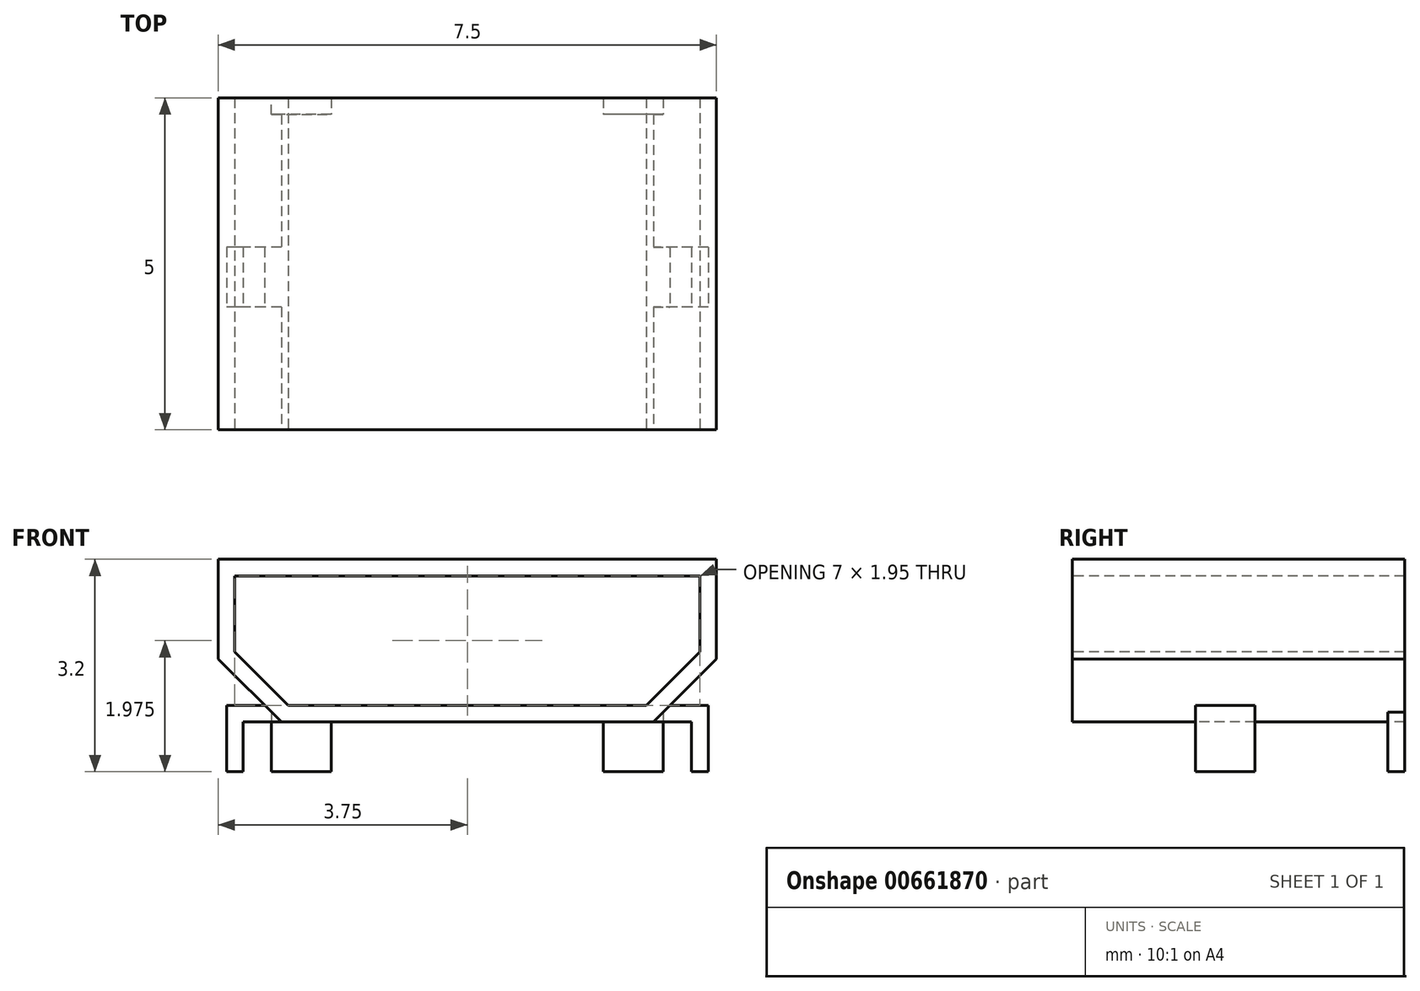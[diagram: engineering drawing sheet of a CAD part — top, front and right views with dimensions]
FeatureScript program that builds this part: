
annotation { "Feature Type Name" : "Feature", "Feature Type Description" : "" }
export const myFeature = defineFeature(function(context is Context, id is Id, definition is map)
    precondition{}
    {
        {
            var Q0;
            Q0=qCreatedBy(makeId("Front.planeOp"),FACE);
            var sketch = newSketch(context, id + "F0", { "sketchPlane" : qUnion([Q0])});
            skLineSegment(sketch, "E0", {"start": v(0, 0) * mm, "end": v(2.8, 0) * mm});
            skLineSegment(sketch, "E1", {"start": v(2.8, 0) * mm, "end": v(3.75, 0.95) * mm});
            skLineSegment(sketch, "E2", {"start": v(3.75, 0.95) * mm, "end": v(3.75, 2.45) * mm});
            skLineSegment(sketch, "E3", {"start": v(3.75, 2.45) * mm, "end": v(0, 2.45) * mm});
            skLineSegment(sketch, "E4", {"start": v(0, 2.45) * mm, "end": v(0, 5.13) * mm, "construction": true});
            skLineSegment(sketch, "E5.0", {"start": v(3.5, 2.2) * mm, "end": v(0, 2.2) * mm});
            skLineSegment(sketch, "E5.1", {"start": v(3.5, 1.05) * mm, "end": v(3.5, 2.2) * mm});
            skLineSegment(sketch, "E5.2", {"start": v(2.7, 0.25) * mm, "end": v(3.5, 1.05) * mm});
            skLineSegment(sketch, "E5.3", {"start": v(0, 0.25) * mm, "end": v(2.7, 0.25) * mm});
            skLineSegment(sketch, "E6.MirrorCS", {"start": v(-3.75, 2.45) * mm, "end": v(0, 2.45) * mm});
            skLineSegment(sketch, "E7.MirrorCS", {"start": v(-3.5, 2.2) * mm, "end": v(0, 2.2) * mm});
            skLineSegment(sketch, "E8.MirrorCS", {"start": v(-3.5, 1.05) * mm, "end": v(-3.5, 2.2) * mm});
            skLineSegment(sketch, "E9.MirrorCS", {"start": v(-3.75, 0.95) * mm, "end": v(-3.75, 2.45) * mm});
            skLineSegment(sketch, "E10.MirrorCS", {"start": v(-2.7, 0.25) * mm, "end": v(-3.5, 1.05) * mm});
            skLineSegment(sketch, "E11.MirrorCS", {"start": v(-2.8, 0) * mm, "end": v(-3.75, 0.95) * mm});
            skLineSegment(sketch, "E12.MirrorCS", {"start": v(0, 0.25) * mm, "end": v(-2.7, 0.25) * mm});
            skLineSegment(sketch, "E13.MirrorCS", {"start": v(0, 0) * mm, "end": v(-2.8, 0) * mm});
            skLineSegment(sketch, "E14", {"start": v(0, 2.2) * mm, "end": v(0, 0.25) * mm, "construction": true});
            skCircle(sketch, "E15", {"center": v(0, 1.23) * mm, "radius": 0.97 * mm, "construction": true});
            skSolve(sketch);
        }
        {
            var Q0;
            Q0=makeQuery(id+"F0.imprint","IMPRINT",FACE,{"disambiguationData":[TD([[makeQuery(id+"F0.imprint","IMPRINT",EDGE,{"derivedFrom":sQuery(id+"F0.wireOp",EDGE,"E0")}),1.0]])]});
            extrude(context, id + "F1", {"entities" : qUnion([Q0]), "oppositeDirection" : true, "depth" : 5 * mm, "offsetDistance" : 25 * mm});
        }
        {
            var Q0;
            Q0=makeQuery(id+"F1.opExtrude","CAP_FACE",FACE,{"disambiguationData":[OSD([sQuery(id+"F0.wireOp",EDGE,"E0"),sQuery(id+"F0.wireOp",EDGE,"E1"),sQuery(id+"F0.wireOp",EDGE,"E2"),sQuery(id+"F0.wireOp",EDGE,"E3"),sQuery(id+"F0.wireOp",EDGE,"E5.0"),sQuery(id+"F0.wireOp",EDGE,"E5.1"),sQuery(id+"F0.wireOp",EDGE,"E5.2"),sQuery(id+"F0.wireOp",EDGE,"E5.3"),sQuery(id+"F0.wireOp",EDGE,"E6.MirrorCS"),sQuery(id+"F0.wireOp",EDGE,"E7.MirrorCS"),sQuery(id+"F0.wireOp",EDGE,"E8.MirrorCS"),sQuery(id+"F0.wireOp",EDGE,"E9.MirrorCS"),sQuery(id+"F0.wireOp",EDGE,"E10.MirrorCS"),sQuery(id+"F0.wireOp",EDGE,"E11.MirrorCS"),sQuery(id+"F0.wireOp",EDGE,"E12.MirrorCS"),sQuery(id+"F0.wireOp",EDGE,"E13.MirrorCS")])],"isStart":false});
            cPlane(context, id + "F2", {"entities" : qUnion([Q0]), "cplaneType" : CPlaneType.OFFSET, "offset" : 2.7 * mm, "oppositeDirection" : true, "width" : 150 * mm, "height" : 150 * mm});
        }
        {
            var Q0;
            Q0=qCreatedBy(id+"F2.planeOp",FACE);
            var sketch = newSketch(context, id + "F3", { "sketchPlane" : qUnion([Q0])});
            skLineSegment(sketch, "E16", {"start": v(-3.62, -0.75) * mm, "end": v(-3.62, 0.25) * mm});
            skLineSegment(sketch, "E17", {"start": v(-3.62, 0.25) * mm, "end": v(3.62, 0.25) * mm});
            skLineSegment(sketch, "E18", {"start": v(3.62, 0.25) * mm, "end": v(3.62, -0.75) * mm});
            skLineSegment(sketch, "E19", {"start": v(0, 0) * mm, "end": v(0, -1.12) * mm, "construction": true});
            skLineSegment(sketch, "E20", {"start": v(-3.5, 0.25) * mm, "end": v(-3.5, -0.75) * mm, "construction": true});
            skLineSegment(sketch, "E21", {"start": v(-3.62, -0.75) * mm, "end": v(-3.38, -0.75) * mm});
            skLineSegment(sketch, "E22", {"start": v(-3.38, -0.75) * mm, "end": v(-3.38, 0) * mm});
            skLineSegment(sketch, "E23", {"start": v(-3.38, 0) * mm, "end": v(3.38, 0) * mm});
            skLineSegment(sketch, "E24", {"start": v(3.38, 0) * mm, "end": v(3.38, -0.75) * mm});
            skLineSegment(sketch, "E25", {"start": v(3.38, -0.75) * mm, "end": v(3.62, -0.75) * mm});
            skSolve(sketch);
        }
        {
            var Q0;
            Q0 = qSketchRegion(id + "F3", true);
            extrude(context, id + "F4", {"entities" : qUnion([Q0]), "operationType" : NewBodyOperationType.ADD, "depth" : 0.9 * mm, "offsetDistance" : 25 * mm, "symmetric" : true});
        }
        {
            var Q0;
            Q0=makeQuery(id+"F1.opExtrude","CAP_FACE",FACE,{"disambiguationData":[OSD([sQuery(id+"F0.wireOp",EDGE,"E0"),sQuery(id+"F0.wireOp",EDGE,"E1"),sQuery(id+"F0.wireOp",EDGE,"E2"),sQuery(id+"F0.wireOp",EDGE,"E3"),sQuery(id+"F0.wireOp",EDGE,"E5.0"),sQuery(id+"F0.wireOp",EDGE,"E5.1"),sQuery(id+"F0.wireOp",EDGE,"E5.2"),sQuery(id+"F0.wireOp",EDGE,"E5.3"),sQuery(id+"F0.wireOp",EDGE,"E6.MirrorCS"),sQuery(id+"F0.wireOp",EDGE,"E7.MirrorCS"),sQuery(id+"F0.wireOp",EDGE,"E8.MirrorCS"),sQuery(id+"F0.wireOp",EDGE,"E9.MirrorCS"),sQuery(id+"F0.wireOp",EDGE,"E10.MirrorCS"),sQuery(id+"F0.wireOp",EDGE,"E11.MirrorCS"),sQuery(id+"F0.wireOp",EDGE,"E12.MirrorCS"),sQuery(id+"F0.wireOp",EDGE,"E13.MirrorCS")])],"isStart":false});
            var sketch = newSketch(context, id + "F5", { "sketchPlane" : qUnion([Q0])});
            skLineSegment(sketch, "E26", {"start": v(-2.95, 0.25) * mm, "end": v(-2.95, -0.75) * mm});
            skLineSegment(sketch, "E27", {"start": v(-2.95, -0.75) * mm, "end": v(-2.05, -0.75) * mm});
            skLineSegment(sketch, "E28", {"start": v(-2.05, -0.75) * mm, "end": v(-2.05, 0.25) * mm});
            skLineSegment(sketch, "E29", {"start": v(-2.05, 0.25) * mm, "end": v(-2.95, 0.25) * mm});
            skLineSegment(sketch, "E30", {"start": v(0, 0) * mm, "end": v(0, -1) * mm, "construction": true});
            skLineSegment(sketch, "E31", {"start": v(-2.5, -0.75) * mm, "end": v(-2.5, 0.25) * mm, "construction": true});
            skLineSegment(sketch, "E32.MirrorCS", {"start": v(2.05, 0.25) * mm, "end": v(2.95, 0.25) * mm});
            skLineSegment(sketch, "E33.MirrorCS", {"start": v(2.95, 0.25) * mm, "end": v(2.95, -0.75) * mm});
            skLineSegment(sketch, "E34.MirrorCS", {"start": v(2.95, -0.75) * mm, "end": v(2.05, -0.75) * mm});
            skLineSegment(sketch, "E35.MirrorCS", {"start": v(2.05, -0.75) * mm, "end": v(2.05, 0.25) * mm});
            skSolve(sketch);
        }
        {
            var Q0;
            Q0 = qSketchRegion(id + "F5", true);
            extrude(context, id + "F6", {"entities" : qUnion([Q0]), "operationType" : NewBodyOperationType.ADD, "oppositeDirection" : true, "depth" : 0.25 * mm, "offsetDistance" : 25 * mm});
        }
        {
            var Q0;
            Q0=makeQuery(id+"F4.boolean.opBoolean","MERGE",FACE,{"derivedFrom":[makeQuery(id+"F1.opExtrude","SWEPT_FACE",FACE,{"disambiguationData":[OSD([sQuery(id+"F0.wireOp",EDGE,"E0"),sQuery(id+"F0.wireOp",EDGE,"E13.MirrorCS")])]}),makeQuery(id+"F4.opExtrude","SWEPT_FACE",FACE,{"disambiguationData":[OSD([sQuery(id+"F3.wireOp",EDGE,"E23")])]})]});
            var sketch = newSketch(context, id + "F7", { "sketchPlane" : qUnion([Q0])});
            skLineSegment(sketch, "E36", {"start": v(3.38, -2.3) * mm, "end": v(0, -2.3) * mm, "construction": true});
            skLineSegment(sketch, "E37", {"start": v(0, -2.3) * mm, "end": v(0, 0) * mm, "construction": true});
            skCircle(sketch, "E38", {"center": v(0, -2.3) * mm, "radius": 5 * mm, "construction": true});
            skSolve(sketch);
        }
    });
